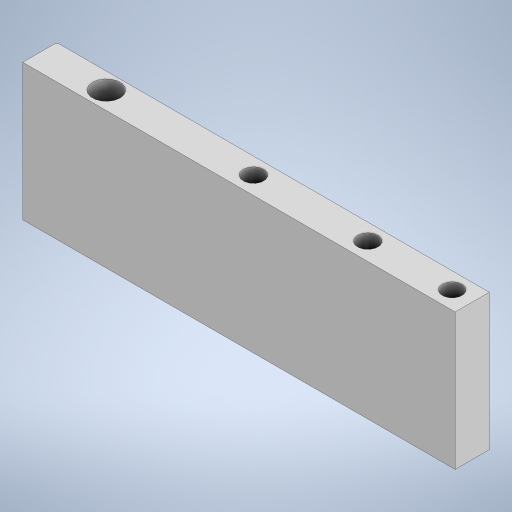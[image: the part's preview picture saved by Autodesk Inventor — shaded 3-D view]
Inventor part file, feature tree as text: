
AUTODESK INVENTOR PART (.ipt)
format: ipt  version: 2024 (Build 280153000, 153)  size: 217,600 bytes
history: native  units: in
note: dims shown in document units (in); Inventor stores cm internally (conversion verified against a paired STEP export)
features: extrude x2, sketch x2, fillet x1
ambient origin geometry x8: Origin, YZ Plane, XZ Plane, XY Plane, X Axis, Y Axis, Z Axis, Center Point
bodies: Solid1 (feature_tree)
feature tree (5):
  extrude  "Extrusion1"  Depth=0.9843in
  fillet  "Face Fillet1"
  extrude  "Extrusion4"  Depth=0.0787in
  sketch  "Sketch1"  dims[d0=12.4803in d1=0.9843in]
  sketch  "Sketch5"  dims[d2=3.937in d3=0.0in d15=0.0787in d16=0.5906in d17=0.5906in d18=3.937in d19=0.0in]
